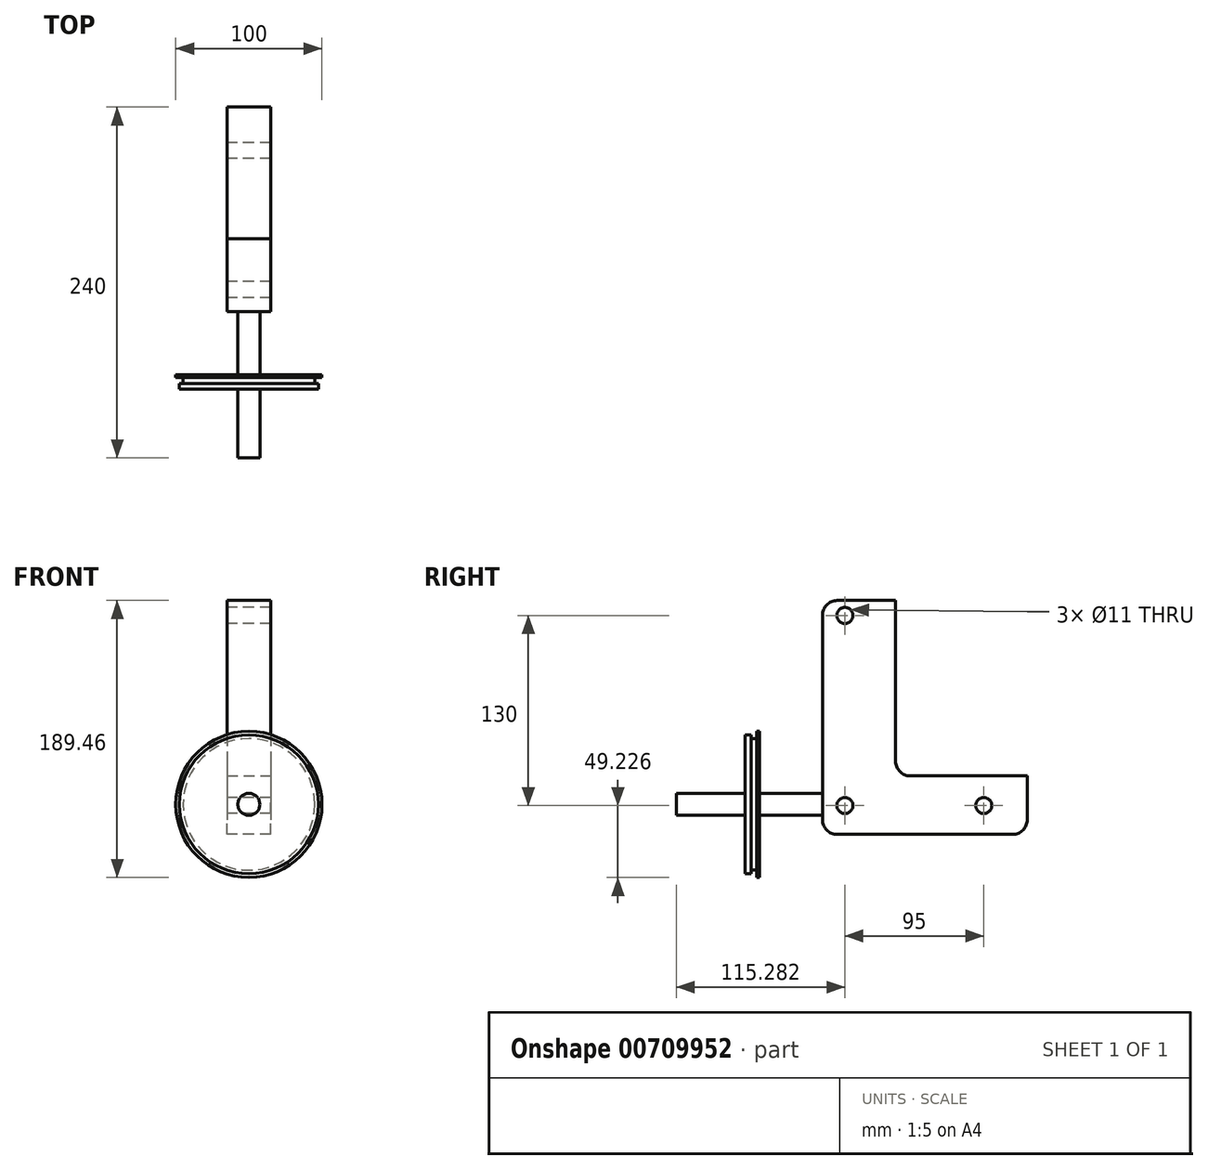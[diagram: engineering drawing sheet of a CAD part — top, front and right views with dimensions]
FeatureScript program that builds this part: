
annotation { "Feature Type Name" : "Feature", "Feature Type Description" : "" }
export const myFeature = defineFeature(function(context is Context, id is Id, definition is map)
    precondition{}
    {
        {
            var Q0;
            Q0=qCreatedBy(makeId("Right.planeOp"),FACE);
            var sketch = newSketch(context, id + "F0", { "sketchPlane" : qUnion([Q0])});
            skCircle(sketch, "E0", {"center": v(-53.39, 118.06) * mm, "radius": 5 * mm});
            skCircle(sketch, "E1", {"center": v(-53.39, -11.94) * mm, "radius": 5 * mm});
            skCircle(sketch, "E2", {"center": v(41.61, -11.94) * mm, "radius": 5 * mm});
            skSolve(sketch);
        }
        {
            var Q0;
            Q0=qCreatedBy(makeId("Right.planeOp"),FACE);
            var sketch = newSketch(context, id + "F1", { "sketchPlane" : qUnion([Q0])});
            skLineSegment(sketch, "E3.bottom", {"start": v(-68.67, 128.3) * mm, "end": v(71.33, 128.3) * mm});
            skLineSegment(sketch, "E3.top", {"start": v(-68.67, -31.7) * mm, "end": v(71.33, -31.7) * mm});
            skLineSegment(sketch, "E3.left", {"start": v(-68.67, 128.3) * mm, "end": v(-68.67, -31.7) * mm});
            skLineSegment(sketch, "E3.right", {"start": v(71.33, 128.3) * mm, "end": v(71.33, -31.7) * mm});
            skSolve(sketch);
        }
        {
            var Q0;
            Q0=makeQuery(id+"F1.imprint","IMPRINT",FACE,{"disambiguationData":[TD([[makeQuery(id+"F1.imprint","IMPRINT",EDGE,{"derivedFrom":sQuery(id+"F1.wireOp",EDGE,"E3.bottom")}),-1.0]])]});
            extrude(context, id + "F2", {"entities" : qUnion([Q0]), "depth" : 30 * mm, "offsetDistance" : 25 * mm});
        }
        {
            var Q0;
            Q0=makeQuery(id+"F2.opExtrude","SWEPT_EDGE",EDGE,{"disambiguationData":[OSD([sQuery(id+"F1.wireOp",EDGE,"E3.bottom"),sQuery(id+"F1.wireOp",EDGE,"E3.left")])]});
            var Q1;
            Q1=makeQuery(id+"F2.opExtrude","SWEPT_EDGE",EDGE,{"disambiguationData":[OSD([sQuery(id+"F1.wireOp",EDGE,"E3.top"),sQuery(id+"F1.wireOp",EDGE,"E3.left")])]});
            fillet(context, id + "F3", {"entities" : qUnion([Q0, Q1]), "radius" : 10 * mm, "tangentPropagation" : true, "allowEdgeOverflow" : false});
        }
        {
            var Q0;
            Q0=makeQuery(id+"F2.opExtrude","CAP_FACE",FACE,{"disambiguationData":[OSD([sQuery(id+"F1.wireOp",EDGE,"E3.bottom"),sQuery(id+"F1.wireOp",EDGE,"E3.top"),sQuery(id+"F1.wireOp",EDGE,"E3.left"),sQuery(id+"F1.wireOp",EDGE,"E3.right")])],"isStart":false});
            var sketch = newSketch(context, id + "F4", { "sketchPlane" : qUnion([Q0])});
            skLineSegment(sketch, "E4.bottom", {"start": v(71.33, 128.3) * mm, "end": v(-18.67, 128.3) * mm});
            skLineSegment(sketch, "E4.top", {"start": v(71.33, 8.3) * mm, "end": v(-18.67, 8.3) * mm});
            skLineSegment(sketch, "E4.left", {"start": v(71.33, 128.3) * mm, "end": v(71.33, 8.3) * mm});
            skLineSegment(sketch, "E4.right", {"start": v(-18.67, 128.3) * mm, "end": v(-18.67, 8.3) * mm});
            skSolve(sketch);
        }
        {
            var Q0;
            Q0=makeQuery(id+"F4.imprint","IMPRINT",FACE,{"disambiguationData":[TD([[makeQuery(id+"F4.imprint","IMPRINT",EDGE,{"derivedFrom":sQuery(id+"F4.wireOp",EDGE,"E4.bottom")}),-1.0]])]});
            extrude(context, id + "F5", {"entities" : qUnion([Q0]), "operationType" : NewBodyOperationType.REMOVE, "endBound" : BoundingType.THROUGH_ALL, "oppositeDirection" : true, "depth" : 25 * mm, "offsetDistance" : 25 * mm});
        }
        {
            var Q0;
            Q0=makeQuery(id+"F5.boolean.opBoolean","COPY",EDGE,{"derivedFrom":makeQuery(id+"F5.opExtrude","SWEPT_EDGE",EDGE,{"disambiguationData":[OSD([sQuery(id+"F1.wireOp",EDGE,"E3.bottom"),sQuery(id+"F4.wireOp",EDGE,"E4.bottom"),sQuery(id+"F4.wireOp",EDGE,"E4.right")])]})});
            var Q1;
            Q1=makeQuery(id+"F5.boolean.opBoolean","COPY",EDGE,{"derivedFrom":makeQuery(id+"F5.opExtrude","SWEPT_EDGE",EDGE,{"disambiguationData":[OSD([sQuery(id+"F4.wireOp",EDGE,"E4.top"),sQuery(id+"F4.wireOp",EDGE,"E4.right")])]})});
            var Q2;
            Q2=makeQuery(id+"F5.boolean.opBoolean","COPY",EDGE,{"derivedFrom":makeQuery(id+"F5.opExtrude","SWEPT_EDGE",EDGE,{"disambiguationData":[OSD([sQuery(id+"F1.wireOp",EDGE,"E3.right"),sQuery(id+"F4.wireOp",EDGE,"E4.top"),sQuery(id+"F4.wireOp",EDGE,"E4.left")])]})});
            var Q3;
            Q3=makeQuery(id+"F2.opExtrude","SWEPT_EDGE",EDGE,{"disambiguationData":[OSD([sQuery(id+"F1.wireOp",EDGE,"E3.top"),sQuery(id+"F1.wireOp",EDGE,"E3.right")])]});
            fillet(context, id + "F6", {"entities" : qUnion([Q0, Q1, Q2, Q3]), "radius" : 10 * mm, "tangentPropagation" : true, "allowEdgeOverflow" : false});
        }
        {
            var Q0;
            Q0=sQuery(id+"F0.wireOp",VERTEX,"E0.center");
            var Q1;
            Q1=sQuery(id+"F0.wireOp",VERTEX,"E1.center");
            var Q2;
            Q2=sQuery(id+"F0.wireOp",VERTEX,"E2.center");
            var Q3;
            Q3=makeQuery(id+"F2.opExtrude","SWEPT_BODY",BODY,{"disambiguationData":[OSD([sQuery(id+"F1.wireOp",EDGE,"E3.bottom"),sQuery(id+"F1.wireOp",EDGE,"E3.top"),sQuery(id+"F1.wireOp",EDGE,"E3.left"),sQuery(id+"F1.wireOp",EDGE,"E3.right")])]});
            hole(context, id + "F7", {"style" : HoleStyle.SIMPLE, "endStyle" : HoleEndStyle.THROUGH, "oppositeDirection" : true, "standardTappedOrClearance" : lookupTablePath({ "standard" : "ISO", "fit" : "Normal", "size" : "M10", "type" : "Clearance" }), "standardBlindInLast" : lookupTablePath({ "fit" : "Standard", "standard" : "ISO", "size" : "M10", "type" : "Clearance" }), "holeDiameter" : 11 * mm, "majorDiameter" : 5 * mm, "isTappedThrough" : true, "tappedDepth" : 12 * mm, "tapClearance" : 3, "startFromSketch" : true, "locations" : qUnion([Q0, Q1, Q2]), "scope" : qUnion([Q3])});
        }
        {
            var Q0;
            Q0=makeQuery(id+"F2.opExtrude","SWEPT_FACE",FACE,{"disambiguationData":[OSD([sQuery(id+"F1.wireOp",EDGE,"E3.left")])]});
            var sketch = newSketch(context, id + "F8", { "sketchPlane" : qUnion([Q0])});
            skCircle(sketch, "E5", {"center": v(15, -11.17) * mm, "radius": 7.5 * mm});
            skPoint(sketch, "E5.centerSnap0", {"position": v(15, -21.7) * mm});
            skSolve(sketch);
        }
        {
            var Q0;
            Q0 = qSketchRegion(id + "F8", true);
            extrude(context, id + "F9", {"entities" : qUnion([Q0]), "operationType" : NewBodyOperationType.ADD, "depth" : 100 * mm, "offsetDistance" : 25 * mm});
        }
        {
            var Q0;
            Q0=makeQuery(id+"F2.opExtrude","SWEPT_FACE",FACE,{"disambiguationData":[OSD([sQuery(id+"F1.wireOp",EDGE,"E3.left")])]});
            cPlane(context, id + "F10", {"entities" : qUnion([Q0]), "cplaneType" : CPlaneType.OFFSET, "offset" : 43 * mm, "width" : 150 * mm, "height" : 150 * mm});
        }
        {
            var Q0;
            Q0=qCreatedBy(id+"F10.planeOp",FACE);
            var sketch = newSketch(context, id + "F11", { "sketchPlane" : qUnion([Q0])});
            skCircle(sketch, "E6", {"center": v(15, -11.17) * mm, "radius": 50 * mm});
            skSolve(sketch);
        }
        {
            var Q0;
            Q0 = qSketchRegion(id + "F11", true);
            extrude(context, id + "F12", {"entities" : qUnion([Q0]), "operationType" : NewBodyOperationType.ADD, "depth" : 2 * mm, "offsetDistance" : 25 * mm});
        }
        {
            var Q0;
            Q0=makeQuery(id+"F12.opExtrude","CAP_FACE",FACE,{"disambiguationData":[OSD([sQuery(id+"F11.wireOp",EDGE,"E6")])],"isStart":false});
            var sketch = newSketch(context, id + "F13", { "sketchPlane" : qUnion([Q0])});
            skCircle(sketch, "E7", {"center": v(15, -11.17) * mm, "radius": 45 * mm});
            skSolve(sketch);
        }
        {
            var Q0;
            Q0=makeQuery(id+"F13.imprint","IMPRINT",FACE,{"disambiguationData":[TD([[makeQuery(id+"F13.imprint","IMPRINT",EDGE,{"derivedFrom":sQuery(id+"F13.wireOp",EDGE,"E7")}),1.0]])]});
            extrude(context, id + "F14", {"entities" : qUnion([Q0]), "operationType" : NewBodyOperationType.ADD, "depth" : 4 * mm, "offsetDistance" : 25 * mm});
        }
        {
            var Q0;
            Q0=makeQuery(id+"F14.opExtrude","CAP_FACE",FACE,{"disambiguationData":[OSD([sQuery(id+"F8.wireOp",EDGE,"E5"),sQuery(id+"F11.wireOp",EDGE,"E6"),sQuery(id+"F13.wireOp",EDGE,"E7")])],"isStart":false});
            var sketch = newSketch(context, id + "F15", { "sketchPlane" : qUnion([Q0])});
            skCircle(sketch, "E8", {"center": v(15, -11.17) * mm, "radius": 47.5 * mm});
            skSolve(sketch);
        }
        {
            var Q0;
            Q0 = qSketchRegion(id + "F15", true);
            var Q1;
            Q1=sQuery(id+"F15.wireOp",EDGE,"E8");
            extrude(context, id + "F16", {"entities" : qUnion([Q0]), "operationType" : NewBodyOperationType.ADD, "surfaceEntities" : qUnion([Q1]), "depth" : 4 * mm, "offsetDistance" : 25 * mm});
        }
    });
